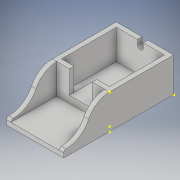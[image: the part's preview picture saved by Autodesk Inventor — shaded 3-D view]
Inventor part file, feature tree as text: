
AUTODESK INVENTOR PART (.ipt)
format: ipt  version: 2018 (Build 220112000, 112)  size: 164,864 bytes
history: native  units: in
note: dims shown in document units (in); Inventor stores cm internally (conversion verified against a paired STEP export)
features: sketch x9, extrude x6, shell x1
ambient origin geometry x8: Origin, YZ Plane, XZ Plane, XY Plane, X Axis, Y Axis, Z Axis, Center Point
bodies: Solid1 (feature_tree)
feature tree (16):
  extrude  "Extrusion1"  Depth=1.1024in
  sketch  "Sketch2"  dims[d4=0.0787in d5=0.7874in]
  shell  "Shell1"  Thickness=0.5906in
  sketch  "Sketch3"  dims[d6=0.0787in d7=0.0394in]
  extrude  "Extrusion2"  Depth=0.7874in
  sketch  "Sketch5"  dims[d11=0.9843in d12=0.0in d13=0.8268in]
  sketch  "Sketch6"  dims[d14=0.7874in d15=0.1969in]
  extrude  "Extrusion3"  Depth=0.0394in
  sketch  "Sketch7"  dims[d16=0.0787in]
  sketch  "Sketch8"  dims[d17=0.1969in]
  extrude  "Extrusion4"  Depth=0.0984in
  extrude  "Extrusion5"  Depth=0.8268in
  extrude  "Extrusion6"  Depth=0.1969in
  sketch  "Sketch1"  dims[d0=0.9843in d1=1.1024in d2=0.5906in d3=0.0in]
  sketch  "Sketch4"  dims[d8=0.9843in d9=0.0in d10=0.0984in]
  sketch  "Sketch9"  dims[d18=0.0787in d19=0.9843in d20=0.0in d21=0.3937in d22=0.0in d23=0.3937in d24=0.3937in d25=0.3937in d26=0.0in]
